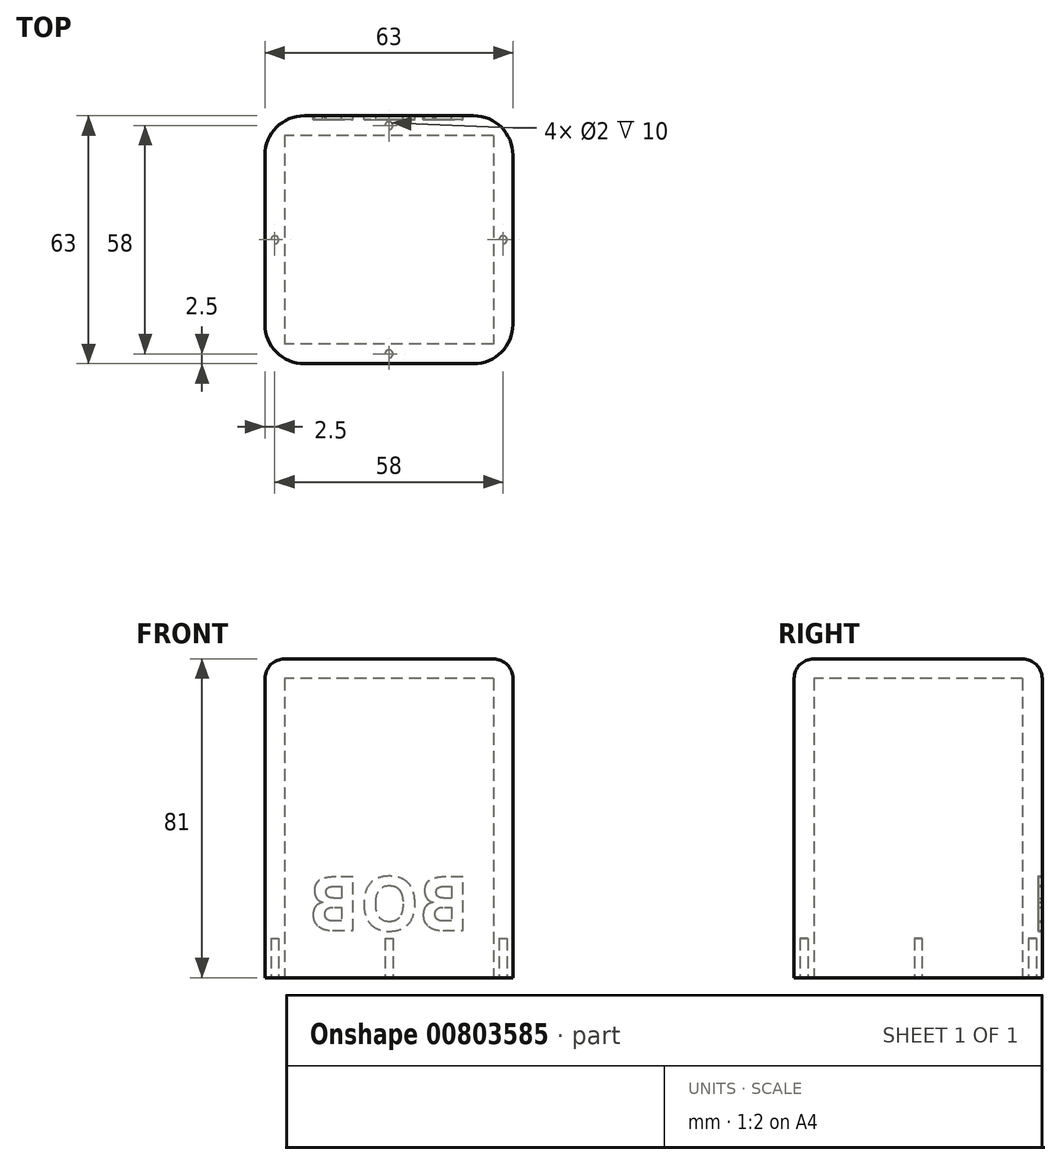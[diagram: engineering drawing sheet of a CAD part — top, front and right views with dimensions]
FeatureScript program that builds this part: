
annotation { "Feature Type Name" : "Feature", "Feature Type Description" : "" }
export const myFeature = defineFeature(function(context is Context, id is Id, definition is map)
    precondition{}
    {
        {
            var Q0;
            Q0=qCreatedBy(makeId("Top.planeOp"),FACE);
            var sketch = newSketch(context, id + "F0", { "sketchPlane" : qUnion([Q0])});
            skLineSegment(sketch, "E0.bottom", {"start": v(31.5, -31.5) * mm, "end": v(-31.5, -31.5) * mm});
            skLineSegment(sketch, "E0.top", {"start": v(31.5, 31.5) * mm, "end": v(-31.5, 31.5) * mm});
            skLineSegment(sketch, "E0.left", {"start": v(31.5, -31.5) * mm, "end": v(31.5, 31.5) * mm});
            skLineSegment(sketch, "E0.right", {"start": v(-31.5, -31.5) * mm, "end": v(-31.5, 31.5) * mm});
            skPoint(sketch, "E0.middle", {"position": v(0, 0) * mm});
            skSolve(sketch);
        }
        {
            var Q0;
            Q0 = qSketchRegion(id + "F0", true);
            extrude(context, id + "F1", {"entities" : qUnion([Q0]), "depth" : 81 * mm, "offsetDistance" : 25 * mm});
        }
        {
            var Q0;
            Q0=makeQuery(id+"F1.opExtrude","CAP_FACE",FACE,{"disambiguationData":[OSD([sQuery(id+"F0.wireOp",EDGE,"E0.bottom"),sQuery(id+"F0.wireOp",EDGE,"E0.top"),sQuery(id+"F0.wireOp",EDGE,"E0.left"),sQuery(id+"F0.wireOp",EDGE,"E0.right")])],"isStart":true});
            var sketch = newSketch(context, id + "F2", { "sketchPlane" : qUnion([Q0])});
            skLineSegment(sketch, "E1.bottom", {"start": v(26.5, -26.5) * mm, "end": v(-26.5, -26.5) * mm});
            skLineSegment(sketch, "E1.top", {"start": v(26.5, 26.5) * mm, "end": v(-26.5, 26.5) * mm});
            skLineSegment(sketch, "E1.left", {"start": v(26.5, -26.5) * mm, "end": v(26.5, 26.5) * mm});
            skLineSegment(sketch, "E1.right", {"start": v(-26.5, -26.5) * mm, "end": v(-26.5, 26.5) * mm});
            skPoint(sketch, "E1.middle", {"position": v(0, 0) * mm});
            skSolve(sketch);
        }
        {
            var Q0;
            Q0 = qSketchRegion(id + "F2", true);
            var Q1;
            Q1=makeQuery(id+"F1.opExtrude","CAP_FACE",FACE,{"disambiguationData":[OSD([sQuery(id+"F0.wireOp",EDGE,"E0.bottom"),sQuery(id+"F0.wireOp",EDGE,"E0.top"),sQuery(id+"F0.wireOp",EDGE,"E0.left"),sQuery(id+"F0.wireOp",EDGE,"E0.right")])],"isStart":false});
            extrude(context, id + "F3", {"entities" : qUnion([Q0]), "operationType" : NewBodyOperationType.REMOVE, "endBound" : BoundingType.UP_TO_SURFACE, "oppositeDirection" : true, "depth" : 48 * mm, "endBoundEntityFace" : qUnion([Q1]), "hasOffset" : true, "offsetDistance" : 5 * mm});
        }
        {
            var Q0;
            Q0=makeQuery(id+"F1.opExtrude","CAP_FACE",FACE,{"disambiguationData":[OSD([sQuery(id+"F0.wireOp",EDGE,"E0.bottom"),sQuery(id+"F0.wireOp",EDGE,"E0.top"),sQuery(id+"F0.wireOp",EDGE,"E0.left"),sQuery(id+"F0.wireOp",EDGE,"E0.right")])],"isStart":true});
            var sketch = newSketch(context, id + "F4", { "sketchPlane" : qUnion([Q0])});
            skCircle(sketch, "E2", {"center": v(-29, 0) * mm, "radius": 1 * mm});
            skPoint(sketch, "E2.centerSnap0", {"position": v(-31.5, 0) * mm});
            skCircle(sketch, "E3", {"center": v(0, 29) * mm, "radius": 1 * mm});
            skPoint(sketch, "E3.centerSnap0", {"position": v(0, 31.5) * mm});
            skCircle(sketch, "E4", {"center": v(29, 0) * mm, "radius": 1 * mm});
            skPoint(sketch, "E4.centerSnap0", {"position": v(31.5, 0) * mm});
            skCircle(sketch, "E5", {"center": v(0, -29) * mm, "radius": 1 * mm});
            skPoint(sketch, "E5.centerSnap0", {"position": v(0, -31.5) * mm});
            skSolve(sketch);
        }
        {
            var Q0;
            Q0 = qSketchRegion(id + "F4", true);
            extrude(context, id + "F5", {"entities" : qUnion([Q0]), "operationType" : NewBodyOperationType.REMOVE, "oppositeDirection" : true, "depth" : 10 * mm, "offsetDistance" : 25 * mm});
        }
        {
            var Q0;
            Q0=makeQuery(id+"F1.opExtrude","SWEPT_EDGE",EDGE,{"disambiguationData":[OSD([sQuery(id+"F0.wireOp",EDGE,"E0.bottom"),sQuery(id+"F0.wireOp",EDGE,"E0.right")])]});
            var Q1;
            Q1=makeQuery(id+"F1.opExtrude","SWEPT_EDGE",EDGE,{"disambiguationData":[OSD([sQuery(id+"F0.wireOp",EDGE,"E0.top"),sQuery(id+"F0.wireOp",EDGE,"E0.right")])]});
            var Q2;
            Q2=makeQuery(id+"F1.opExtrude","SWEPT_EDGE",EDGE,{"disambiguationData":[OSD([sQuery(id+"F0.wireOp",EDGE,"E0.top"),sQuery(id+"F0.wireOp",EDGE,"E0.left")])]});
            var Q3;
            Q3=makeQuery(id+"F1.opExtrude","SWEPT_EDGE",EDGE,{"disambiguationData":[OSD([sQuery(id+"F0.wireOp",EDGE,"E0.bottom"),sQuery(id+"F0.wireOp",EDGE,"E0.left")])]});
            fillet(context, id + "F6", {"entities" : qUnion([Q0, Q1, Q2, Q3]), "radius" : 10 * mm, "tangentPropagation" : true, "allowEdgeOverflow" : false});
        }
        {
            var Q0;
            Q0=makeQuery(id+"F1.opExtrude","CAP_FACE",FACE,{"disambiguationData":[OSD([sQuery(id+"F0.wireOp",EDGE,"E0.bottom"),sQuery(id+"F0.wireOp",EDGE,"E0.top"),sQuery(id+"F0.wireOp",EDGE,"E0.left"),sQuery(id+"F0.wireOp",EDGE,"E0.right")])],"isStart":false});
            fillet(context, id + "F7", {"entities" : qUnion([Q0]), "radius" : 5 * mm, "tangentPropagation" : true, "allowEdgeOverflow" : false});
        }
        {
            var Q0;
            Q0=makeQuery(id+"F1.opExtrude","SWEPT_FACE",FACE,{"disambiguationData":[OSD([sQuery(id+"F0.wireOp",EDGE,"E0.top")])]});
            var sketch = newSketch(context, id + "F8", { "sketchPlane" : qUnion([Q0])});
            skText(sketch, "E6", { "text": "BOB", "fontName": "OpenSans-Bold.ttf"});
            const initialGuessF8  = {"E6": [-0.0205, 0.012, 1, 0, 0.01372]};
            skSetInitialGuess(sketch, initialGuessF8);
            skSolve(sketch);
        }
        {
            var Q0;
            Q0 = qSketchRegion(id + "F8", true);
            extrude(context, id + "F9", {"entities" : qUnion([Q0]), "operationType" : NewBodyOperationType.REMOVE, "oppositeDirection" : true, "depth" : 1 * mm, "offsetDistance" : 25 * mm});
        }
    });
